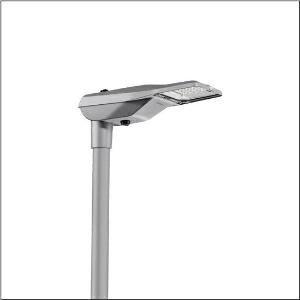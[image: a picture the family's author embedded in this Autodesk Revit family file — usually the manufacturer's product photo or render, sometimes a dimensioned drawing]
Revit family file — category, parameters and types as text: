
# Revit family: streetlight_sl_21_iq_micro___st1_0ab_5xe1m31y08db_79d8
name_source: partatom
category: Lighting Fixtures
units: mm (PartAtom-declared; Revit-internal decimal feet)

## family parameters
Cut with Voids When Loaded = No
Host = Face
Light Source = No
Part Type = Normal
Room Calculation Point = No
Round Connector Dimension = Use Diameter
Shared = No

## types (1)
- --- (1 x LED, 4490 lm, 39.1 W, 3000K)
    Apparent Load = 39 VA
    CIE Flux Codes = 38 73 97 100 100
    Color Rendering = 70
    Color Temperature = 3000K
    Default Elevation = 1800 mm
    Description = Streetlight SL 21 iQ micro, mast luminaire, primary light control with lens, of PMMA, primary optical cover: cover, of toughened safety glass, transparent, light distribution: ST1.0aB, light emission: direct distribution, primary light characteristic: asymmetric, installation type: post-top, side-entry, LED, High Power LED, rated luminous flux: 4.490lm, luminous efficacy: 115lm/W, light colour: 730, colour temperature: 3000K, control: presetting dimming logarithmic, Street-Remote, Auto-Match, Temp-Guard, Lumen-Switch, Night-Set, Smart-Wire, Light-Fading, Desk-Remote (wireless, voltage-free reading and setting of iQ features in the workshop via application-optimized NFC function/RFID function), optimised constant luminous flux control (CLO 2.0), mains connection: 220..240V, AC, 50/60Hz, start of lifetime: 39W, end of service life: 41W, reduction: 17W, luminaire housing, of diecast aluminium, powder-coated, Siteco® metallic grey (DB 702S), corrosivity category C5 mid according to DIN EN ISO 12944, please order mast flange separately, inclination adjustable: 0°, 5°, 10°, 15°, sealing non-destructively replaceable, multi-level sealing system, length: 528mm, width: 235mm, height: 110mm, mast flange for spigot size: 42mm (side-entry): 5XC10008XM4, 60/48mm (side-entry/post-top): 5XC10108XM2, 76/60mm (side-entry/post-top): 5XC10108XM1, Smart Interface below and above, protection rating (complete): IP66, insulation class (complete): insulation class II (safety insulation), certification: CE, ENEC, ENEC+, VDE, impact resistance: IK09, permissible operating ambient temperature for outdoor applications: -40..+50°C, standard-compliant lighting for roads and squares, packaging unit: 1 piece

Light Distribution: ST1.0aB
    Height = 110 mm
    Lamp = 1 x LED
    Lamp Light Flux = 4490 lm
    Lamp Power = 39.1 W
    Lamp count = 1
    Length = 528 mm
    Luminous efficacy = 115 lm/W
    Manufacturer = Siteco
    ModVariant = No
    Model = 5XE1M31Y08DB
    Number of Poles = 1
    OnlyDefault = Yes
    Power Factor = 1
    Product Name = Streetlight SL 21 iQ micro | ST1.0aB
    Product group = mast luminaire | pylon top
    ProductGroupID = 6100
    Protection Class = Protection class II
    Protection Degree = IP 66
    RLX_Detail_Level = 1
    RLX_Emergency_Light_Flux = 0 lm
    RLX_Emergency_Type = 0
    RLX_Emergency_Type_DB = No
    RlxData = <blob elided: 98357 chars, md5=e7cc74d8>
    Socket = socket
    Standby Power = 0 W
    System Light Flux = 4490 lm
    System Power = 39 W
    Type Comments = factory setting: luminous flux: 100 % | dim-lin: 254 | 765 mA
    Type Image = l_1007239.jpg
    URL = http://relux.com
    VarID = @adj_042717
    Voltage = 0 V
    Weight = 0.00 kg
    Width = 235 mm

## geometry (parser evidence)
native form markers: Blend x4, Sweep x10
no freeform markers — native parametric forms only
